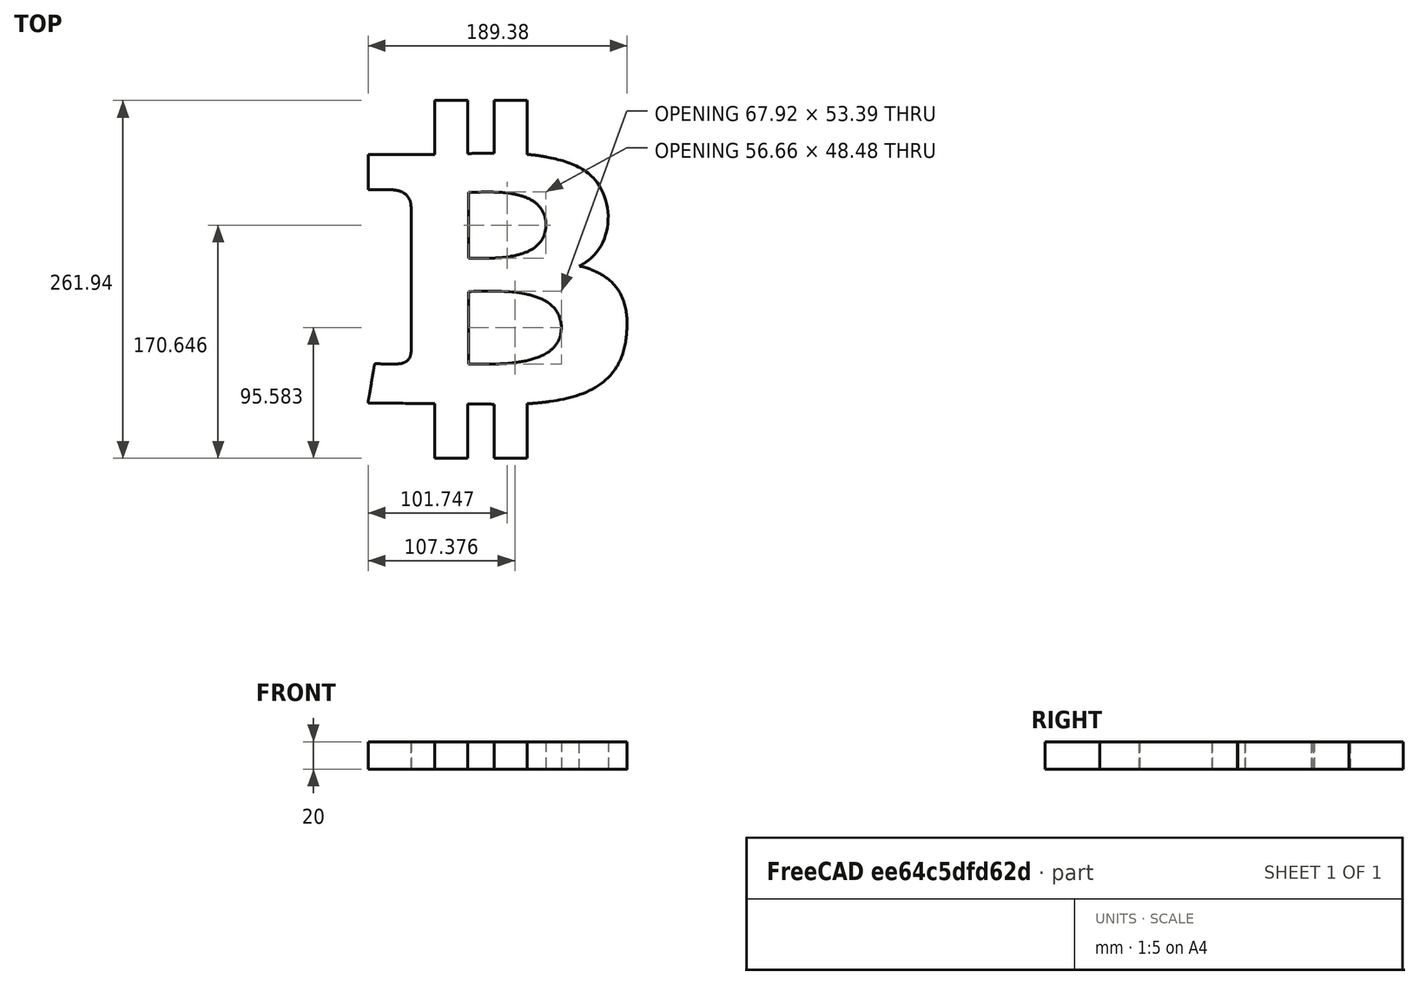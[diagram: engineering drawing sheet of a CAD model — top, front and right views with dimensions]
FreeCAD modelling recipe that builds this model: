
FCSTD DOCUMENT  (FreeCAD 0.19R24415 (Git))
Label: btc_clock
License: All rights reserved
LicenseURL: http://en.wikipedia.org/wiki/All_rights_reserved
objects: Part::FeaturePython×4, Part::Feature×3, Sketcher::SketchObject×1, Part::Extrusion×1, App::DocumentObjectGroup×1, Mesh::Feature×1
note: 9 computed .brp shape members not serialized (recipe doc carries the construction recipe); baked Part::Feature solids carry a one-line shape summary decoded from their .brp

FEATURE [Part::Feature] path249
  shape: bbox 379.5 x 523.9 x 2e-07 mm, 1 faces, 0 solids (baked)
FEATURE [Part::Feature] path249001
  shape: bbox 118.8 x 98.91 x 2e-07 mm, 1 faces, 0 solids (baked)
FEATURE [Part::Feature] path249002
  shape: bbox 139.3 x 109.2 x 2e-07 mm, 1 faces, 0 solids (baked)
FEATURE [Part::FeaturePython] Cutout  # WARN: FeaturePython — macro-defined, semantics opaque (R4)
  Base = -> path249
  Refine = true
  Tolerance = 0
  Tool = -> path249001
FEATURE [Part::FeaturePython] Cutout001  # WARN: FeaturePython — macro-defined, semantics opaque (R4)
  Base = -> Cutout
  Refine = true
  Tolerance = 0
  Tool = -> path249002
FEATURE [Part::FeaturePython] Connect  # WARN: FeaturePython — macro-defined, semantics opaque (R4)
  Objects = -> [Cutout001]
  Refine = true
  Tolerance = 0
FEATURE [Part::FeaturePython] Clone  label="Connect001"  # Draft clone (typed FeaturePython)
  AttacherType = Attacher::AttachEngine3D
  Fuse = false
  Objects = -> [Connect]
  Scale = (0.5,0.5,0.5)
FEATURE [Sketcher::SketchObject] Sketch
  FullyConstrained = false
  sketch-geometry (56):
    g0: BSplineCurve PolesCount=2 KnotsCount=2 Degree=1 IsPeriodic=0
    g1: BSplineCurve PolesCount=2 KnotsCount=2 Degree=1 IsPeriodic=0
    g2: BSplineCurve PolesCount=2 KnotsCount=2 Degree=1 IsPeriodic=0
    g3: BSplineCurve PolesCount=4 KnotsCount=2 Degree=3 IsPeriodic=0
    g4: BSplineCurve PolesCount=4 KnotsCount=2 Degree=3 IsPeriodic=0
    g5: BSplineCurve PolesCount=4 KnotsCount=2 Degree=3 IsPeriodic=0
    g6: BSplineCurve PolesCount=2 KnotsCount=2 Degree=1 IsPeriodic=0
    g7: BSplineCurve PolesCount=2 KnotsCount=2 Degree=1 IsPeriodic=0
    g8: BSplineCurve PolesCount=2 KnotsCount=2 Degree=1 IsPeriodic=0
    g9: BSplineCurve PolesCount=4 KnotsCount=2 Degree=3 IsPeriodic=0
    g10: BSplineCurve PolesCount=4 KnotsCount=2 Degree=3 IsPeriodic=0
    g11: BSplineCurve PolesCount=4 KnotsCount=2 Degree=3 IsPeriodic=0
    g12: BSplineCurve PolesCount=4 KnotsCount=2 Degree=3 IsPeriodic=0
    g13: BSplineCurve PolesCount=4 KnotsCount=2 Degree=3 IsPeriodic=0
    g14: BSplineCurve PolesCount=2 KnotsCount=2 Degree=1 IsPeriodic=0
    g15: BSplineCurve PolesCount=2 KnotsCount=2 Degree=1 IsPeriodic=0
    g16: BSplineCurve PolesCount=4 KnotsCount=2 Degree=3 IsPeriodic=0
    g17: BSplineCurve PolesCount=2 KnotsCount=2 Degree=1 IsPeriodic=0
    g18: BSplineCurve PolesCount=2 KnotsCount=2 Degree=1 IsPeriodic=0
    g19: BSplineCurve PolesCount=2 KnotsCount=2 Degree=1 IsPeriodic=0
    g20: BSplineCurve PolesCount=2 KnotsCount=2 Degree=1 IsPeriodic=0
    g21: BSplineCurve PolesCount=2 KnotsCount=2 Degree=1 IsPeriodic=0
    g22: BSplineCurve PolesCount=2 KnotsCount=2 Degree=1 IsPeriodic=0
    g23: BSplineCurve PolesCount=2 KnotsCount=2 Degree=1 IsPeriodic=0
    g24: BSplineCurve PolesCount=2 KnotsCount=2 Degree=1 IsPeriodic=0
    g25: BSplineCurve PolesCount=4 KnotsCount=2 Degree=3 IsPeriodic=0
    g26: BSplineCurve PolesCount=4 KnotsCount=2 Degree=3 IsPeriodic=0
    g27: BSplineCurve PolesCount=4 KnotsCount=2 Degree=3 IsPeriodic=0
    g28: BSplineCurve PolesCount=4 KnotsCount=2 Degree=3 IsPeriodic=0
    g29: BSplineCurve PolesCount=4 KnotsCount=2 Degree=3 IsPeriodic=0
    g30: BSplineCurve PolesCount=4 KnotsCount=2 Degree=3 IsPeriodic=0
    g31: BSplineCurve PolesCount=2 KnotsCount=2 Degree=1 IsPeriodic=0
    g32: BSplineCurve PolesCount=4 KnotsCount=2 Degree=3 IsPeriodic=0
    g33: BSplineCurve PolesCount=4 KnotsCount=2 Degree=3 IsPeriodic=0
    g34: BSplineCurve PolesCount=4 KnotsCount=2 Degree=3 IsPeriodic=0
    g35: BSplineCurve PolesCount=4 KnotsCount=2 Degree=3 IsPeriodic=0
    g36: BSplineCurve PolesCount=2 KnotsCount=2 Degree=1 IsPeriodic=0
    g37: BSplineCurve PolesCount=2 KnotsCount=2 Degree=1 IsPeriodic=0
    g38: BSplineCurve PolesCount=2 KnotsCount=2 Degree=1 IsPeriodic=0
    g39: BSplineCurve PolesCount=2 KnotsCount=2 Degree=1 IsPeriodic=0
    g40: BSplineCurve PolesCount=2 KnotsCount=2 Degree=1 IsPeriodic=0
    g41: BSplineCurve PolesCount=2 KnotsCount=2 Degree=1 IsPeriodic=0
    g42: BSplineCurve PolesCount=4 KnotsCount=2 Degree=3 IsPeriodic=0
    g43: BSplineCurve PolesCount=2 KnotsCount=2 Degree=1 IsPeriodic=0
    g44: BSplineCurve PolesCount=4 KnotsCount=2 Degree=3 IsPeriodic=0
    g45: BSplineCurve PolesCount=4 KnotsCount=2 Degree=3 IsPeriodic=0
    g46: BSplineCurve PolesCount=4 KnotsCount=2 Degree=3 IsPeriodic=0
    g47: BSplineCurve PolesCount=4 KnotsCount=2 Degree=3 IsPeriodic=0
    g48: BSplineCurve PolesCount=4 KnotsCount=2 Degree=3 IsPeriodic=0
    g49: BSplineCurve PolesCount=4 KnotsCount=2 Degree=3 IsPeriodic=0
    g50: BSplineCurve PolesCount=2 KnotsCount=2 Degree=1 IsPeriodic=0
    g51: BSplineCurve PolesCount=4 KnotsCount=2 Degree=3 IsPeriodic=0
    g52: BSplineCurve PolesCount=4 KnotsCount=2 Degree=3 IsPeriodic=0
    g53: BSplineCurve PolesCount=4 KnotsCount=2 Degree=3 IsPeriodic=0
    g54: BSplineCurve PolesCount=4 KnotsCount=2 Degree=3 IsPeriodic=0
    g55: BSplineCurve PolesCount=4 KnotsCount=2 Degree=3 IsPeriodic=0
  constraints (56):
    c: Coincident(g0,g1)
    c: Coincident(g1,g2)
    c: Coincident(g2,g3)
    c: Coincident(g3,g4)
    c: Coincident(g4,g5)
    c: Coincident(g5,g6)
    c: Coincident(g6,g7)
    c: Coincident(g7,g8)
    c: Coincident(g8,g9)
    c: Coincident(g9,g10)
    c: Coincident(g10,g11)
    c: Coincident(g11,g12)
    c: Coincident(g12,g13)
    c: Coincident(g13,g14)
    c: Coincident(g14,g15)
    c: Coincident(g15,g16)
    c: Coincident(g16,g17)
    c: Coincident(g17,g18)
    c: Coincident(g18,g19)
    c: Coincident(g19,g20)
    c: Coincident(g20,g21)
    c: Coincident(g21,g22)
    c: Coincident(g22,g23)
    c: Coincident(g23,g24)
    c: Coincident(g24,g25)
    c: Coincident(g25,g26)
    c: Coincident(g26,g27)
    c: Coincident(g27,g28)
    c: Coincident(g28,g29)
    c: Coincident(g29,g30)
    c: Coincident(g30,g31)
    c: Coincident(g31,g32)
    c: Coincident(g32,g33)
    c: Coincident(g33,g34)
    c: Coincident(g34,g35)
    c: Coincident(g35,g36)
    c: Coincident(g36,g37)
    c: Coincident(g37,g38)
    c: Coincident(g38,g39)
    c: Coincident(g39,g40)
    c: Coincident(g40,g41)
    c: Coincident(g41,g0)
    c: Coincident(g42,g43)
    c: Coincident(g43,g44)
    c: Coincident(g44,g45)
    c: Coincident(g45,g46)
    c: Coincident(g46,g47)
    c: Coincident(g47,g48)
    c: Coincident(g48,g42)
    c: Coincident(g49,g50)
    c: Coincident(g50,g51)
    c: Coincident(g51,g52)
    c: Coincident(g52,g53)
    c: Coincident(g53,g54)
    c: Coincident(g54,g55)
    c: Coincident(g55,g49)
FEATURE [Part::Extrusion] Extrude  label="B_Logo"
  Base = -> Sketch
  Dir = (0,0,1)
  DirMode = 2
  FaceMakerClass = Part::FaceMakerBullseye
  LengthFwd = 20
  LengthRev = 0
  Solid = true
  Symmetric = false
FEATURE [App::DocumentObjectGroup] Gruppe  label="import_svg"
  Group = -> [Clone,Connect]
FEATURE [Mesh::Feature] Mesh  label="B_Logo (Meshed)"
